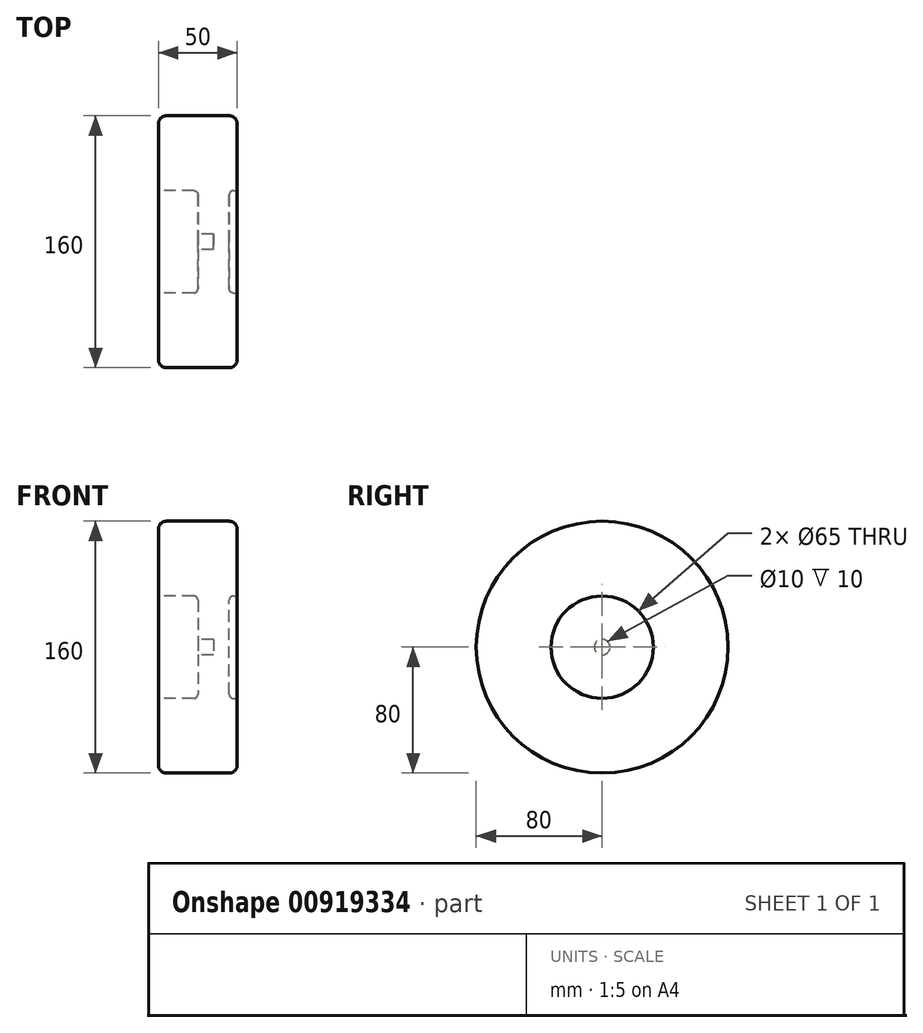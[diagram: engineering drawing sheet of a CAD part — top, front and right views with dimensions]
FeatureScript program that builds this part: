
annotation { "Feature Type Name" : "Feature", "Feature Type Description" : "" }
export const myFeature = defineFeature(function(context is Context, id is Id, definition is map)
    precondition{}
    {
        {
            var Q0;
            Q0=qCreatedBy(makeId("Right.planeOp"),FACE);
            var sketch = newSketch(context, id + "F0", { "sketchPlane" : qUnion([Q0])});
            skCircle(sketch, "E0", {"center": v(0, 0) * mm, "radius": 80 * mm});
            skSolve(sketch);
        }
        {
            var Q0;
            Q0 = qSketchRegion(id + "F0", true);
            extrude(context, id + "F1", {"entities" : qUnion([Q0]), "depth" : 50 * mm, "offsetDistance" : 25 * mm});
        }
        {
            var Q0;
            Q0=makeQuery(id+"F1.opExtrude","CAP_FACE",FACE,{"disambiguationData":[OSD([sQuery(id+"F0.wireOp",EDGE,"E0")])],"isStart":false});
            var sketch = newSketch(context, id + "F2", { "sketchPlane" : qUnion([Q0])});
            skCircle(sketch, "E1", {"center": v(0, 0) * mm, "radius": 32.5 * mm});
            skSolve(sketch);
        }
        {
            var Q0;
            Q0=makeQuery(id+"F2.imprint","IMPRINT",FACE,{"disambiguationData":[TD([[makeQuery(id+"F2.imprint","IMPRINT",EDGE,{"derivedFrom":sQuery(id+"F2.wireOp",EDGE,"E1")}),1.0]])]});
            extrude(context, id + "F3", {"entities" : qUnion([Q0]), "operationType" : NewBodyOperationType.REMOVE, "oppositeDirection" : true, "depth" : 5 * mm, "offsetDistance" : 25 * mm});
        }
        {
            var Q0;
            Q0=makeQuery(id+"F1.opExtrude","CAP_FACE",FACE,{"disambiguationData":[OSD([sQuery(id+"F0.wireOp",EDGE,"E0")])],"isStart":true});
            var sketch = newSketch(context, id + "F4", { "sketchPlane" : qUnion([Q0])});
            skCircle(sketch, "E2", {"center": v(0, 0) * mm, "radius": 32.5 * mm});
            skSolve(sketch);
        }
        {
            var Q0;
            Q0=makeQuery(id+"F4.imprint","IMPRINT",FACE,{"disambiguationData":[TD([[makeQuery(id+"F4.imprint","IMPRINT",EDGE,{"derivedFrom":sQuery(id+"F4.wireOp",EDGE,"E2")}),1.0]])]});
            extrude(context, id + "F5", {"entities" : qUnion([Q0]), "operationType" : NewBodyOperationType.REMOVE, "oppositeDirection" : true, "depth" : 25 * mm, "offsetDistance" : 25 * mm});
        }
        {
            var Q0;
            Q0=makeQuery(id+"F5.boolean.opBoolean","COPY",FACE,{"derivedFrom":makeQuery(id+"F5.opExtrude","CAP_FACE",FACE,{"disambiguationData":[OSD([sQuery(id+"F4.wireOp",EDGE,"E2")])],"isStart":false})});
            var sketch = newSketch(context, id + "F6", { "sketchPlane" : qUnion([Q0])});
            skCircle(sketch, "E3", {"center": v(0, 0) * mm, "radius": 5 * mm});
            skSolve(sketch);
        }
        {
            var Q0;
            Q0=makeQuery(id+"F6.imprint","IMPRINT",FACE,{"disambiguationData":[TD([[makeQuery(id+"F6.imprint","IMPRINT",EDGE,{"derivedFrom":sQuery(id+"F6.wireOp",EDGE,"E3")}),1.0]])]});
            extrude(context, id + "F7", {"entities" : qUnion([Q0]), "operationType" : NewBodyOperationType.REMOVE, "oppositeDirection" : true, "depth" : 10 * mm, "offsetDistance" : 25 * mm});
        }
        {
            var Q0;
            Q0=makeQuery(id+"F1.opExtrude","CAP_EDGE",EDGE,{"disambiguationData":[OSD([sQuery(id+"F0.wireOp",EDGE,"E0")])],"isStart":true});
            var Q1;
            Q1=makeQuery(id+"F1.opExtrude","CAP_EDGE",EDGE,{"disambiguationData":[OSD([sQuery(id+"F0.wireOp",EDGE,"E0")])],"isStart":false});
            fillet(context, id + "F8", {"entities" : qUnion([Q0, Q1]), "radius" : 5 * mm, "tangentPropagation" : true, "allowEdgeOverflow" : false});
        }
        {
            var Q0;
            Q0=makeQuery(id+"F3.boolean.opBoolean","COPY",EDGE,{"derivedFrom":makeQuery(id+"F3.opExtrude","CAP_EDGE",EDGE,{"disambiguationData":[OSD([sQuery(id+"F2.wireOp",EDGE,"E1")])],"isStart":true})});
            var Q1;
            Q1=makeQuery(id+"F3.boolean.opBoolean","COPY",EDGE,{"derivedFrom":makeQuery(id+"F3.opExtrude","CAP_EDGE",EDGE,{"disambiguationData":[OSD([sQuery(id+"F2.wireOp",EDGE,"E1")])],"isStart":false})});
            var Q2;
            Q2=makeQuery(id+"F5.boolean.opBoolean","COPY",EDGE,{"derivedFrom":makeQuery(id+"F5.opExtrude","CAP_EDGE",EDGE,{"disambiguationData":[OSD([sQuery(id+"F4.wireOp",EDGE,"E2")])],"isStart":true})});
            var Q3;
            Q3=makeQuery(id+"F5.boolean.opBoolean","COPY",EDGE,{"derivedFrom":makeQuery(id+"F5.opExtrude","CAP_EDGE",EDGE,{"disambiguationData":[OSD([sQuery(id+"F4.wireOp",EDGE,"E2")])],"isStart":false})});
            fillet(context, id + "F9", {"entities" : qUnion([Q0, Q1, Q2, Q3]), "radius" : 2.5 * mm, "tangentPropagation" : true, "allowEdgeOverflow" : false});
        }
    });
